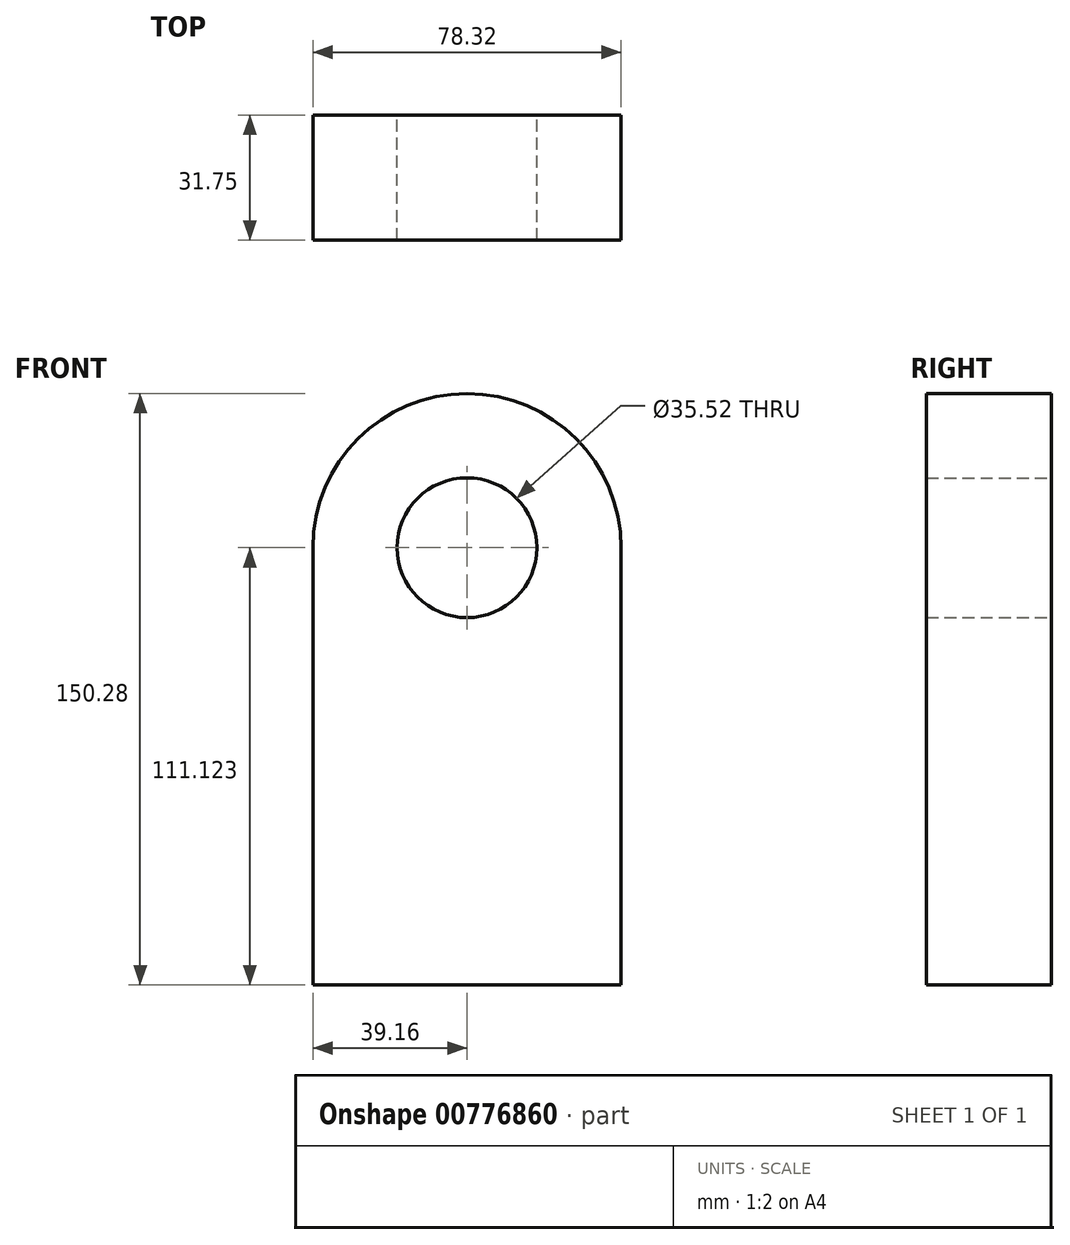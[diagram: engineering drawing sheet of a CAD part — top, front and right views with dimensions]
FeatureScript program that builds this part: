
annotation { "Feature Type Name" : "Feature", "Feature Type Description" : "" }
export const myFeature = defineFeature(function(context is Context, id is Id, definition is map)
    precondition{}
    {
        {
            var Q0;
            Q0=qCreatedBy(makeId("Front.planeOp"),FACE);
            var sketch = newSketch(context, id + "F0", { "sketchPlane" : qUnion([Q0])});
            skLineSegment(sketch, "E0.top", {"start": v(-39.16, -55.56) * mm, "end": v(39.16, -55.56) * mm});
            skLineSegment(sketch, "E0.left", {"start": v(-39.16, 55.56) * mm, "end": v(-39.16, -55.56) * mm});
            skLineSegment(sketch, "E0.right", {"start": v(39.16, 55.56) * mm, "end": v(39.16, -55.56) * mm});
            skPoint(sketch, "E0.middle", {"position": v(0, 0) * mm});
            skArc(sketch, "E1", {"start": v(39.16, 55.56) * mm, "mid": v(0, 94.72) * mm, "end": v(-39.16, 55.56) * mm});
            skCircle(sketch, "E2", {"center": v(0, 55.56) * mm, "radius": 17.76 * mm});
            skSolve(sketch);
        }
        {
            var Q0;
            Q0=makeQuery(id+"F0.imprint","IMPRINT",FACE,{"disambiguationData":[TD([[makeQuery(id+"F0.imprint","IMPRINT",EDGE,{"derivedFrom":sQuery(id+"F0.wireOp",EDGE,"E0.top")}),1.0]])]});
            extrude(context, id + "F1", {"entities" : qUnion([Q0]), "depth" : 31.75 * mm, "offsetDistance" : 25.4 * mm});
        }
    });
